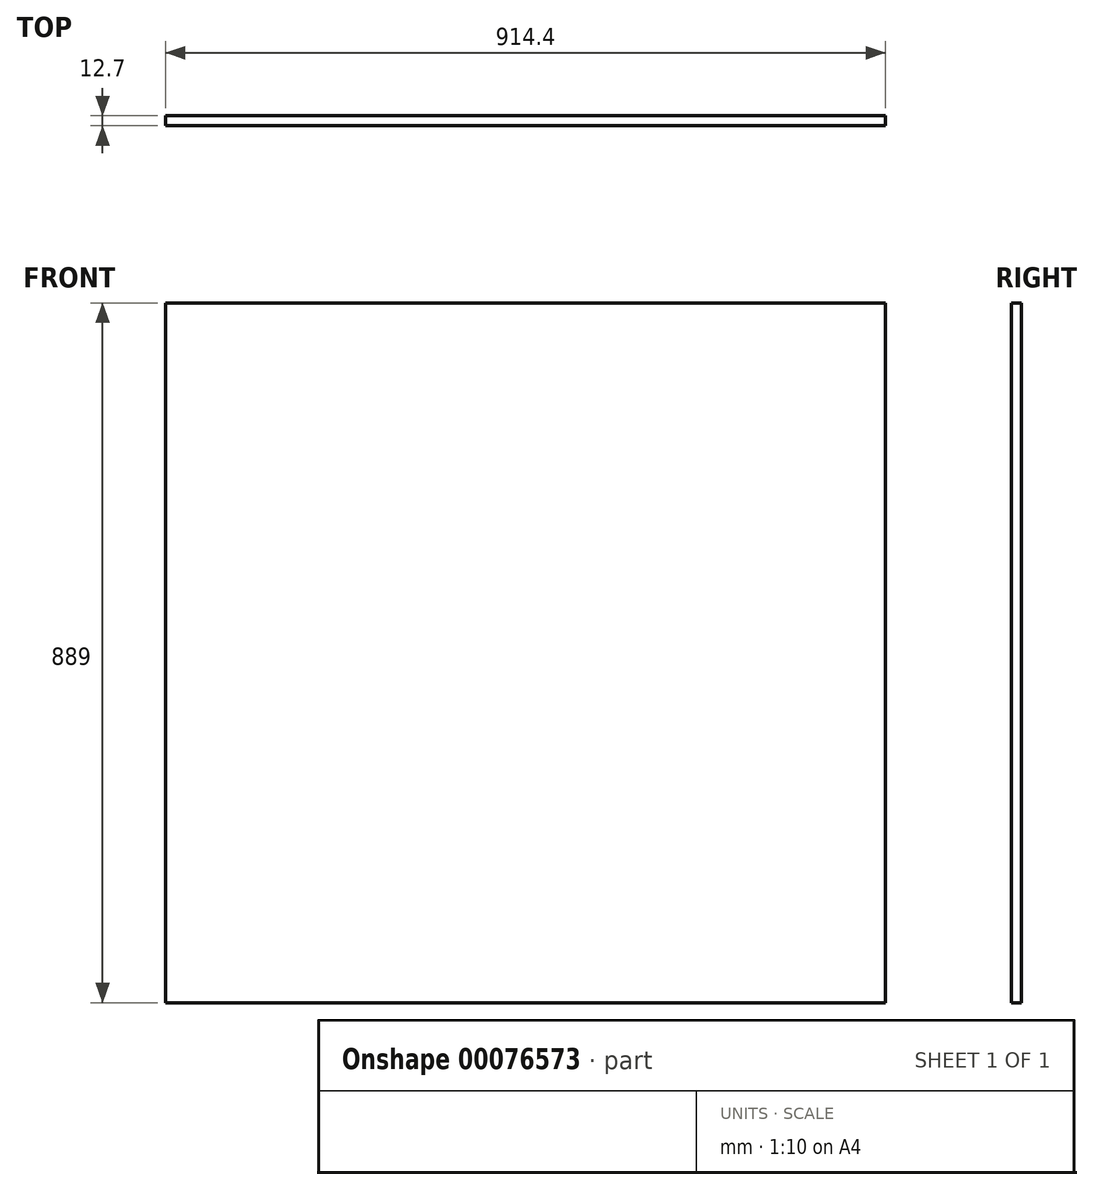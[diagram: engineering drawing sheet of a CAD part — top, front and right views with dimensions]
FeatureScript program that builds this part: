
annotation { "Feature Type Name" : "Feature", "Feature Type Description" : "" }
export const myFeature = defineFeature(function(context is Context, id is Id, definition is map)
    precondition{}
    {
        {
            var Q0;
            Q0=qCreatedBy(makeId("Front.planeOp"),FACE);
            var sketch = newSketch(context, id + "F0", { "sketchPlane" : qUnion([Q0])});
            skLineSegment(sketch, "E0.bottom", {"start": v(0, 0) * mm, "end": v(914.4, 0) * mm});
            skLineSegment(sketch, "E0.top", {"start": v(0, 889) * mm, "end": v(914.4, 889) * mm});
            skLineSegment(sketch, "E0.left", {"start": v(0, 0) * mm, "end": v(0, 889) * mm});
            skLineSegment(sketch, "E0.right", {"start": v(914.4, 0) * mm, "end": v(914.4, 889) * mm});
            skSolve(sketch);
        }
        {
            var Q0;
            Q0=makeQuery(id+"F0.imprint","IMPRINT",FACE,{"disambiguationData":[TD([[makeQuery(id+"F0.imprint","IMPRINT",EDGE,{"derivedFrom":sQuery(id+"F0.wireOp",EDGE,"E0.bottom")}),1.0]])]});
            extrude(context, id + "F1", {"entities" : qUnion([Q0]), "endBound" : BoundingType.SYMMETRIC, "depth" : 12.7 * mm});
        }
    });
